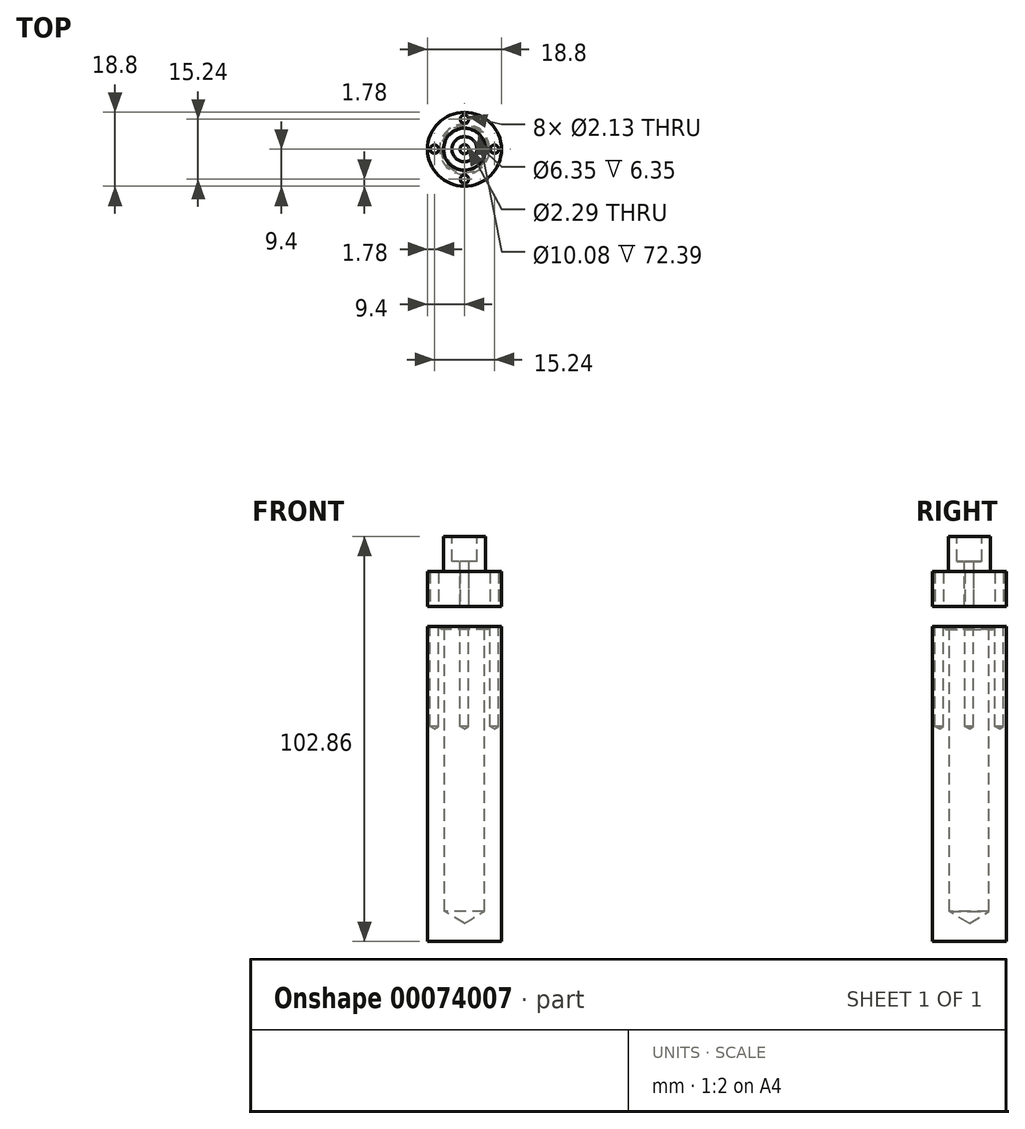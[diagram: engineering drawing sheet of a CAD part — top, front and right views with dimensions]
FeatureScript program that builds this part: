
annotation { "Feature Type Name" : "Feature", "Feature Type Description" : "" }
export const myFeature = defineFeature(function(context is Context, id is Id, definition is map)
    precondition{}
    {
        {
            var Q0;
            Q0=qCreatedBy(makeId("Front.planeOp"),FACE);
            var sketch = newSketch(context, id + "F0", { "sketchPlane" : qUnion([Q0])});
            skLineSegment(sketch, "E0.rect.bottom", {"start": v(-30, 12.7) * mm, "end": v(30, 12.7) * mm});
            skLineSegment(sketch, "E0.rect.top", {"start": v(-30, -12.7) * mm, "end": v(30, -12.7) * mm});
            skLineSegment(sketch, "E0.rect.left", {"start": v(-30, 12.7) * mm, "end": v(-30, -12.7) * mm});
            skLineSegment(sketch, "E0.rect.right", {"start": v(30, 12.7) * mm, "end": v(30, -12.7) * mm});
            skPoint(sketch, "E0.rect.middle", {"position": v(0, 0) * mm});
            skLineSegment(sketch, "E1.rect.bottom", {"start": v(-10, 12.7) * mm, "end": v(10, 12.7) * mm});
            skLineSegment(sketch, "E1.rect.top", {"start": v(-10, -12.7) * mm, "end": v(10, -12.7) * mm});
            skLineSegment(sketch, "E1.rect.left", {"start": v(-10, 12.7) * mm, "end": v(-10, -12.7) * mm});
            skLineSegment(sketch, "E1.rect.right", {"start": v(10, 12.7) * mm, "end": v(10, -12.7) * mm});
            skLineSegment(sketch, "E2.bottom", {"start": v(0, -12.7) * mm, "end": v(10, -12.7) * mm});
            skLineSegment(sketch, "E2.top", {"start": v(0, -142.7) * mm, "end": v(10, -142.7) * mm});
            skLineSegment(sketch, "E2.left", {"start": v(0, -12.7) * mm, "end": v(0, -142.7) * mm});
            skLineSegment(sketch, "E2.right", {"start": v(10, -12.7) * mm, "end": v(10, -142.7) * mm});
            skLineSegment(sketch, "E3", {"start": v(0, -77.7) * mm, "end": v(55.85, -77.7) * mm, "construction": true});
            skPoint(sketch, "E3.endSnap0", {"position": v(10, -77.7) * mm});
            skLineSegment(sketch, "E4.MirrorCS", {"start": v(-30, -168.1) * mm, "end": v(30, -168.1) * mm});
            skLineSegment(sketch, "E5.MirrorCS", {"start": v(-30, -168.1) * mm, "end": v(-30, -142.7) * mm});
            skLineSegment(sketch, "E6.MirrorCS", {"start": v(-30, -142.7) * mm, "end": v(30, -142.7) * mm});
            skLineSegment(sketch, "E7.MirrorCS", {"start": v(-10, -168.1) * mm, "end": v(-10, -142.7) * mm});
            skLineSegment(sketch, "E8.MirrorCS", {"start": v(10, -168.1) * mm, "end": v(10, -142.7) * mm});
            skLineSegment(sketch, "E9.MirrorCS", {"start": v(30, -168.1) * mm, "end": v(30, -142.7) * mm});
            skLineSegment(sketch, "E10", {"start": v(15, -12.7) * mm, "end": v(15, -142.7) * mm});
            skLineSegment(sketch, "E11", {"start": v(0, 34.44) * mm, "end": v(0, -179.82) * mm, "construction": true});
            skPoint(sketch, "E11.startSnap0", {"position": v(0, 12.7) * mm});
            skPoint(sketch, "E11.endSnap0", {"position": v(0, -168.1) * mm});
            skSolve(sketch);
        }
        {
            var Q0;
            Q0=qCreatedBy(makeId("Front.planeOp"),FACE);
            var sketch = newSketch(context, id + "F1", { "sketchPlane" : qUnion([Q0])});
            skLineSegment(sketch, "E12", {"start": v(0, 13.52) * mm, "end": v(0, -13.77) * mm, "construction": true});
            skLineSegment(sketch, "E13", {"start": v(5.33, 12.78) * mm, "end": v(5.33, 3.9) * mm});
            skLineSegment(sketch, "E14", {"start": v(5.33, 3.9) * mm, "end": v(9.4, 3.9) * mm});
            skLineSegment(sketch, "E15", {"start": v(9.4, 3.9) * mm, "end": v(9.4, -5) * mm});
            skLineSegment(sketch, "E16", {"start": v(9.4, -5) * mm, "end": v(1.14, -5) * mm});
            skLineSegment(sketch, "E17", {"start": v(1.14, -5) * mm, "end": v(1.14, 6.43) * mm});
            skLineSegment(sketch, "E18", {"start": v(1.14, 6.43) * mm, "end": v(3.18, 6.43) * mm});
            skLineSegment(sketch, "E19", {"start": v(3.18, 6.43) * mm, "end": v(3.18, 12.78) * mm});
            skLineSegment(sketch, "E20", {"start": v(3.18, 12.78) * mm, "end": v(5.33, 12.78) * mm});
            skLineSegment(sketch, "E21.bottom", {"start": v(9.4, -10.08) * mm, "end": v(5.08, -10.08) * mm});
            skLineSegment(sketch, "E21.top", {"start": v(9.4, -90.08) * mm, "end": v(5.08, -90.08) * mm});
            skLineSegment(sketch, "E21.left", {"start": v(9.4, -10.08) * mm, "end": v(9.4, -90.08) * mm});
            skLineSegment(sketch, "E21.right", {"start": v(5.08, -10.08) * mm, "end": v(5.08, -90.08) * mm});
            skLineSegment(sketch, "E22", {"start": v(7.62, -10.08) * mm, "end": v(7.62, -11.95) * mm, "construction": true});
            skLineSegment(sketch, "E23", {"start": v(5.97, -10.08) * mm, "end": v(5.97, -11.6) * mm, "construction": true});
            skCircle(sketch, "E24", {"center": v(5.97, -10.33) * mm, "radius": 0.25 * mm, "construction": true});
            skLineSegment(sketch, "E25", {"start": v(6.4, -10.08) * mm, "end": v(5.97, -10.84) * mm});
            skLineSegment(sketch, "E26.MirrorCS", {"start": v(5.54, -10.08) * mm, "end": v(5.97, -10.84) * mm});
            skPoint(sketch, "E27", {"position": v(5.97, -10.83) * mm});
            skLineSegment(sketch, "E28", {"start": v(5.08, -10.08) * mm, "end": v(0, -10.08) * mm});
            skLineSegment(sketch, "E29", {"start": v(0, -10.08) * mm, "end": v(0, -90.08) * mm});
            skLineSegment(sketch, "E30", {"start": v(5.08, -90.08) * mm, "end": v(0, -90.08) * mm});
            skSolve(sketch);
        }
        {
            var Q0;
            {var subQ0=sQuery(id+"F1.wireOp",EDGE,"CLkmakUS-2P28-UgWZ-2Srl-EtxpEp7xc1pJ");Q0=makeQuery(id+"F1.imprint","IMPRINT",FACE,{"disambiguationData":[TD([[makeQuery(id+"F1.imprint","IMPRINT",EDGE,{"derivedFrom":subQ0}),-1.0]])]});}
            var Q1;
            {var subQ1=sQuery(id+"F1.wireOp",EDGE,"E21.top");Q1=makeQuery(id+"F1.imprint","IMPRINT",FACE,{"disambiguationData":[TD([[makeQuery(id+"F1.imprint","IMPRINT",EDGE,{"derivedFrom":subQ1}),-1.0]])]});}
            var Q2;
            Q2=makeQuery(id+"F1.imprint","IMPRINT",FACE,{"disambiguationData":[TD([[makeQuery(id+"F1.imprint","IMPRINT",EDGE,{"derivedFrom":sQuery(id+"F1.wireOp",EDGE,"E13")}),-1.0]])]});
            var Q3;
            Q3=makeQuery(id+"F1.imprint","IMPRINT",FACE,{"disambiguationData":[TD([[makeQuery(id+"F1.imprint","IMPRINT",EDGE,{"derivedFrom":sQuery(id+"F1.wireOp",EDGE,"E21.right")}),-1.0]])]});
            var Q4;
            Q4=sQuery(id+"F1.wireOp",EDGE,"E12");
            revolve(context, id + "F2", {"entities" : qUnion([Q0, Q1, Q2, Q3]), "axis" : qUnion([Q4]), "revolveType" : RevolveType.FULL});
        }
        {
            var Q0;
            {var subQ0=sQuery(id+"F1.wireOp",EDGE,"E21.bottom");Q0=makeQuery(id+"F2.opRevolve","SWEPT_FACE",FACE,{"disambiguationData":[OSD([subQ0]),TDD([makeQuery(id+"F1.imprint","IMPRINT",EDGE,{"disambiguationData":[TD([[makeQuery(id+"F1.imprint","INTERSECT",VERTEX,{"derivedFrom":[subQ0,sQuery(id+"F1.wireOp",EDGE,"E21.left")]}),-1.0]])],"derivedFrom":subQ0})])]});}
            var sketch = newSketch(context, id + "F3", { "sketchPlane" : qUnion([Q0])});
            skPoint(sketch, "E31.center", {"position": v(0, 0) * mm});
            skLineSegment(sketch, "E32", {"start": v(0, 0) * mm, "end": v(7.62, 0) * mm});
            skCircle(sketch, "E33", {"center": v(7.62, 0) * mm, "radius": 1.07 * mm});
            skCircle(sketch, "E34.1.0", {"center": v(0, 7.62) * mm, "radius": 1.07 * mm});
            skCircle(sketch, "E34.2.0", {"center": v(-7.62, 0) * mm, "radius": 1.07 * mm});
            skCircle(sketch, "E34.3.0", {"center": v(0, -7.62) * mm, "radius": 1.07 * mm});
            skCircle(sketch, "E35", {"center": v(7.62, 0) * mm, "radius": 1.78 * mm});
            skSolve(sketch);
        }
        {
            var Q0;
            Q0=sQuery(id+"F3.wireOp",VERTEX,"E34.2.0.center");
            var Q1;
            Q1=sQuery(id+"F3.wireOp",VERTEX,"E34.1.0.center");
            var Q2;
            Q2=sQuery(id+"F3.wireOp",VERTEX,"E33.center");
            var Q3;
            Q3=sQuery(id+"F3.wireOp",VERTEX,"E34.3.0.center");
            var Q4;
            Q4=makeQuery(id+"F2.opRevolve","SWEPT_BODY",BODY,{"disambiguationData":[OSD([sQuery(id+"F1.wireOp",EDGE,"E21.bottom"),sQuery(id+"F1.wireOp",EDGE,"E21.top"),sQuery(id+"F1.wireOp",EDGE,"E21.left"),sQuery(id+"F1.wireOp",EDGE,"E21.right")])]});
            hole(context, id + "F4", {"style" : HoleStyle.SIMPLE, "holeDiameter" : 2.13 * mm, "endStyle" : HoleEndStyle.BLIND, "holeDepth" : 25.4 * mm, "locations" : qUnion([Q0, Q1, Q2, Q3]), "scope" : qUnion([Q4])});
        }
        {
            var Q0;
            Q0=sQuery(id+"F3.wireOp",VERTEX,"E34.3.0.center");
            var Q1;
            Q1=sQuery(id+"F3.wireOp",VERTEX,"E33.center");
            var Q2;
            Q2=sQuery(id+"F3.wireOp",VERTEX,"E34.1.0.center");
            var Q3;
            Q3=sQuery(id+"F3.wireOp",VERTEX,"E34.2.0.center");
            var Q4;
            Q4=makeQuery(id+"F2.opRevolve","SWEPT_BODY",BODY,{"disambiguationData":[OSD([sQuery(id+"F1.wireOp",EDGE,"E13"),sQuery(id+"F1.wireOp",EDGE,"E14"),sQuery(id+"F1.wireOp",EDGE,"E15"),sQuery(id+"F1.wireOp",EDGE,"E16"),sQuery(id+"F1.wireOp",EDGE,"E17"),sQuery(id+"F1.wireOp",EDGE,"E18"),sQuery(id+"F1.wireOp",EDGE,"E19"),sQuery(id+"F1.wireOp",EDGE,"E20")])]});
            hole(context, id + "F5", {"style" : HoleStyle.SIMPLE, "holeDiameter" : 2.13 * mm, "endStyle" : HoleEndStyle.THROUGH, "oppositeDirection" : true, "locations" : qUnion([Q0, Q1, Q2, Q3]), "scope" : qUnion([Q4]), "isTappedThrough" : true});
        }
        {
            var Q0;
            Q0=sQuery(id+"F3.wireOp",VERTEX,"E31.center");
            var Q1;
            Q1=makeQuery(id+"F2.opRevolve","SWEPT_BODY",BODY,{"disambiguationData":[OSD([sQuery(id+"F1.wireOp",EDGE,"E21.bottom"),sQuery(id+"F1.wireOp",EDGE,"E21.top"),sQuery(id+"F1.wireOp",EDGE,"E21.left"),sQuery(id+"F1.wireOp",EDGE,"E25"),sQuery(id+"F1.wireOp",EDGE,"E26.MirrorCS"),sQuery(id+"F1.wireOp",EDGE,"E28"),sQuery(id+"F1.wireOp",EDGE,"E29"),sQuery(id+"F1.wireOp",EDGE,"E30")])]});
            hole(context, id + "F6", {"style" : HoleStyle.SIMPLE, "endStyle" : HoleEndStyle.BLIND, "holeDiameter" : 10.08 * mm, "holeDepth" : 72.39 * mm, "locations" : qUnion([Q0]), "scope" : qUnion([Q1])});
        }
    });
